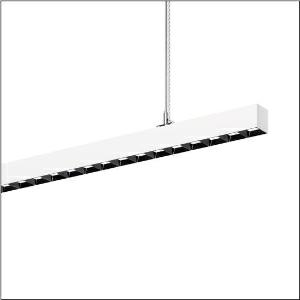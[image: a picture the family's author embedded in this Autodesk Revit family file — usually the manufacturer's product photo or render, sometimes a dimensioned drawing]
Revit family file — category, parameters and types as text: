
# Revit family: silica_r__21_51mx32tctdw_3fbf
name_source: partatom
category: Lighting Fixtures
units: mm (PartAtom-declared; Revit-internal decimal feet)

## family parameters
Cut with Voids When Loaded = No
Host = Face
Light Source = No
Part Type = Normal
Room Calculation Point = No
Round Connector Dimension = Use Diameter
Shared = No

## types (1)
- --- (1 x LED, 15540 lm, 133.6 W, 6500K)
    Apparent Load = 134 VA
    CIE Flux Codes = 84 99 100 60 100
    Color Rendering = 80
    Color Temperature = 6500K
    Default Elevation = 1800 mm
    Description = Silica® 21, office luminaire, primary light control with darklight reflector, of PMMA, black, CAT 2 (L<= 3000cd/m²), light emission: direct/indirect distribution, primary light characteristic: symmetric, installation type: suspended mounting, LED, rated luminous flux: 15.540lm, luminous efficacy: 111lm/W, light colour: 8tw, colour temperature: 2700..6500K, control gear: ECG DALI, with terminal, 3+2-pole, max. 2.5mm², mains connection: 220..240V, AC, 50/60Hz, rated input power: 140.3W, luminaire housing, of aluminium, traffic white (RAL 9016), length: 3.004mm, width: 53mm, height: 53mm, protection rating (complete): IP20, insulation class (complete): insulation class I (protective earthing), certification: CE, permissible operating ambient temperature: 0..+35°C, standard: EN 50419, packaging unit: 1 piece
    Height = 53 mm
    Lamp = 1 x LED
    Lamp Light Flux = 15540 lm
    Lamp Power = 133.6 W
    Lamp count = 1
    Length = 3004 mm
    Luminous efficacy = 116 lm/W
    Manufacturer = Siteco
    ModVariant = No
    Model = 51MX32TCTDW
    Mounting Place = Ceiling
    Mounting Type = Pendant
    Number of Poles = 1
    OnlyDefault = Yes
    Power Factor = 1
    Product Name = Silica® 21
    Product group = office luminaire | ceiling pendant
    ProductGroupID = 902
    Protection Class = Protection class I
    Protection Degree = IP 20
    RLX_Detail_Level = 1
    RLX_Emergency_Light_Flux = 0 lm
    RLX_Emergency_Type = 0
    RLX_Emergency_Type_DB = No
    RlxData = <blob elided: 60941 chars, md5=501c9b69>
    Socket = socket
    Standby Power = 0 W
    System Light Flux = 15540 lm
    System Power = 134 W
    Type Comments = individual setting
    Type Image = l_1313619.jpg
    URL = http://relux.com
    VarID = @adj_089319
    Voltage = 0 V
    Weight = 0.00 kg
    Width = 53 mm

## geometry (parser evidence)
native form markers: Blend x4, Sweep x14
no freeform markers — native parametric forms only
